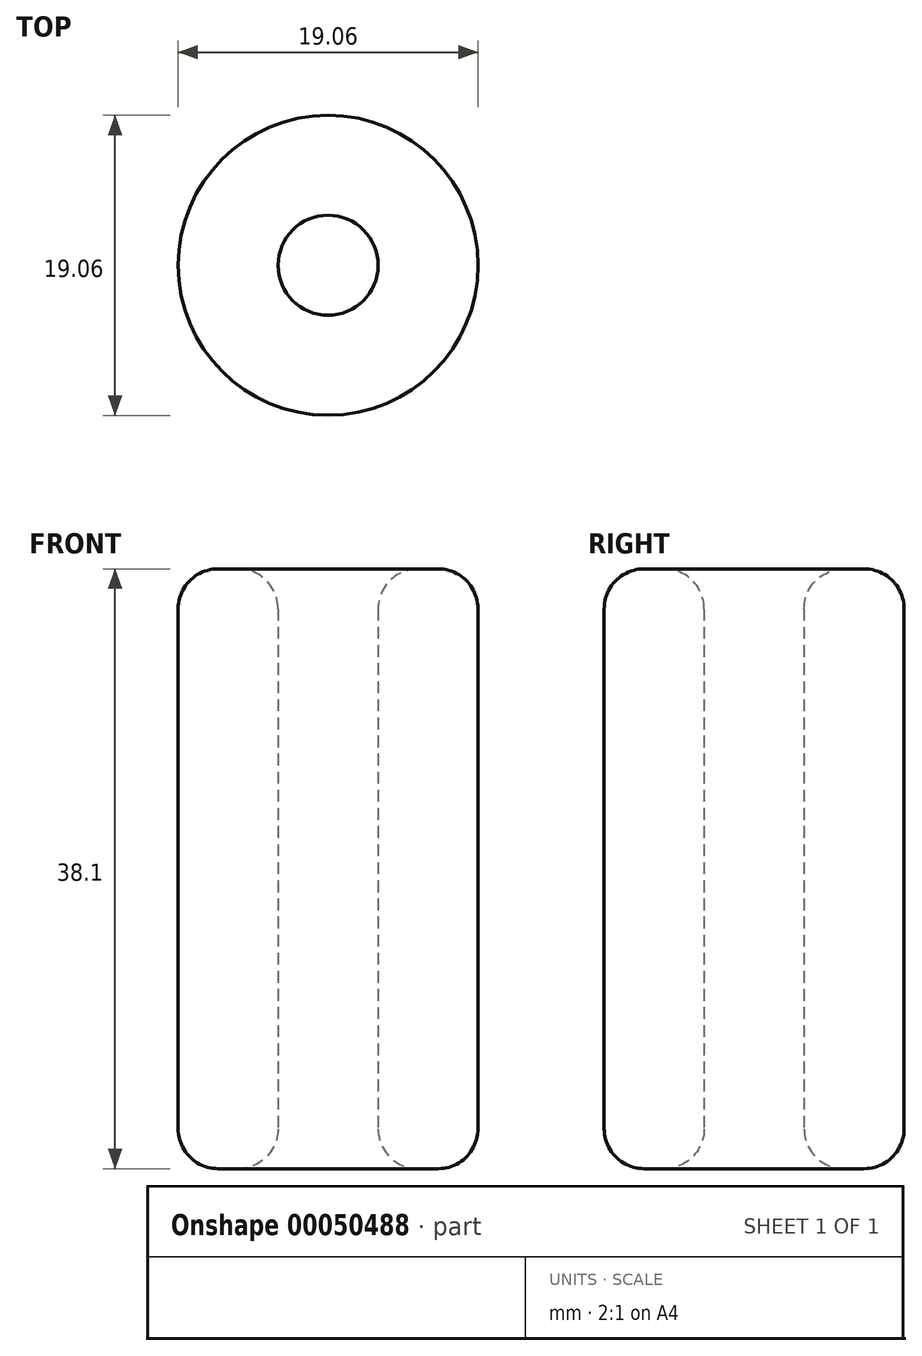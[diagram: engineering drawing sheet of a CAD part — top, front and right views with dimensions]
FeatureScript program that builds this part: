
annotation { "Feature Type Name" : "Feature", "Feature Type Description" : "" }
export const myFeature = defineFeature(function(context is Context, id is Id, definition is map)
    precondition{}
    {
        {
            var Q0;
            Q0=qCreatedBy(makeId("Top.planeOp"),FACE);
            var sketch = newSketch(context, id + "F0", { "sketchPlane" : qUnion([Q0])});
            skCircle(sketch, "E0", {"center": v(0, 0) * mm, "radius": 9.53 * mm});
            skCircle(sketch, "E1", {"center": v(0, 0) * mm, "radius": 3.18 * mm});
            skSolve(sketch);
        }
        {
            var Q0;
            Q0 = qSketchRegion(id + "F0", true);
            extrude(context, id + "F1", {"entities" : qUnion([Q0]), "endBound" : BoundingType.SYMMETRIC, "depth" : 38.1 * mm});
        }
        {
            var Q0;
            Q0=makeQuery(id+"F1.opExtrude","CAP_EDGE",EDGE,{"disambiguationData":[OSD([sQuery(id+"F0.wireOp",EDGE,"E1")])],"isStart":false});
            var Q1;
            Q1=makeQuery(id+"F1.opExtrude","CAP_EDGE",EDGE,{"disambiguationData":[OSD([sQuery(id+"F0.wireOp",EDGE,"E0")])],"isStart":false});
            var Q2;
            Q2=makeQuery(id+"F1.opExtrude","CAP_EDGE",EDGE,{"disambiguationData":[OSD([sQuery(id+"F0.wireOp",EDGE,"E1")])],"isStart":true});
            var Q3;
            Q3=makeQuery(id+"F1.opExtrude","CAP_EDGE",EDGE,{"disambiguationData":[OSD([sQuery(id+"F0.wireOp",EDGE,"E0")])],"isStart":true});
            fillet(context, id + "F2", {"entities" : qUnion([Q0, Q1, Q2, Q3]), "radius" : 2.54 * mm, "tangentPropagation" : true, "allowEdgeOverflow" : false});
        }
    });
